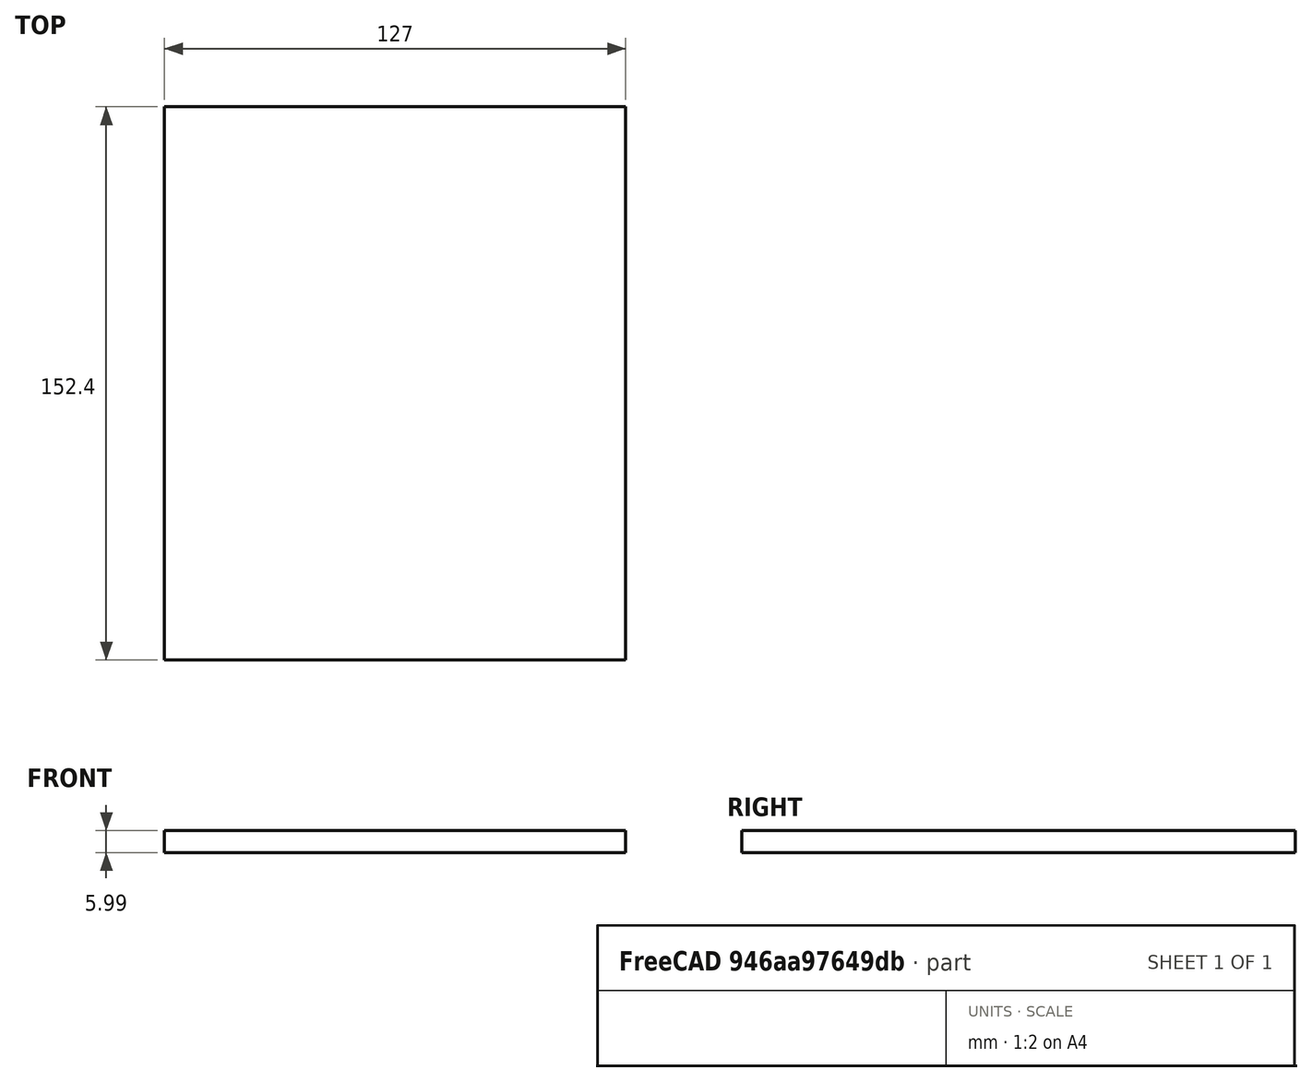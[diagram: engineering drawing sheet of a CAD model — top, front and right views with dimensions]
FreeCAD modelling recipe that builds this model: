
FCSTD DOCUMENT  (FreeCAD 0.19R24267 (Git))
Label: Inv1-P13
License: All rights reserved
LicenseURL: http://en.wikipedia.org/wiki/All_rights_reserved
objects: TechDraw::DrawViewDimension×3, Sketcher::SketchObject×2, TechDraw::DrawProjGroupItem×2, TechDraw::DrawHatch×2, TechDraw::DrawViewAnnotation×2, Part::Extrusion×1, TechDraw::DrawSVGTemplate×1, TechDraw::DrawProjGroup×1, TechDraw::DrawPage×1
note: 3 computed .brp shape members not serialized (recipe doc carries the construction recipe); baked Part::Feature solids carry a one-line shape summary decoded from their .brp

FEATURE [Sketcher::SketchObject] Sketch
  FullyConstrained = true
FEATURE [Sketcher::SketchObject] Sketch001
  FullyConstrained = false
  sketch-geometry (4):
    g0: LineSegment StartX=-70.7971 StartY=53.6303 StartZ=0 EndX=56.2029 EndY=53.6303 EndZ=0
    g1: LineSegment StartX=56.2029 StartY=53.6303 StartZ=0 EndX=56.2029 EndY=-98.7697 EndZ=0
    g2: LineSegment StartX=56.2029 StartY=-98.7697 StartZ=0 EndX=-70.7971 EndY=-98.7697 EndZ=0
    g3: LineSegment StartX=-70.7971 StartY=-98.7697 StartZ=0 EndX=-70.7971 EndY=53.6303 EndZ=0
  constraints (10):
    c: Coincident(g0,g1)
    c: Coincident(g1,g2)
    c: Coincident(g2,g3)
    c: Coincident(g3,g0)
    c: Horizontal(g0)
    c: Horizontal(g2)
    c: Vertical(g1)
    c: Vertical(g3)
    c: DistanceY(g3,g3) = 152.4
    c: DistanceX(g0,g0) = 127
FEATURE [Part::Extrusion] Extrude
  Base = -> Sketch001
  Dir = (0,0,1)
  DirMode = 2
  FaceMakerClass = Part::FaceMakerBullseye
  LengthFwd = 5.9944
  LengthRev = 0
  Solid = true
  Symmetric = false
FEATURE [TechDraw::DrawSVGTemplate] Template
  Height = 215.9
  Orientation = 1
  Width = 279.4
FEATURE [TechDraw::DrawProjGroupItem] ProjItem  label="Front"
  CoarseView = false
  Direction = (0,0,-1)
  Focus = 100
  HardHidden = false
  IsoCount = 0
  IsoHidden = false
  IsoVisible = false
  LockPosition = true
  Perspective = false
  Rotation = 0
  RotationVector = (1,0,0)
  Scale = 0.5
  ScaleType = 2
  SeamHidden = false
  SeamVisible = true
  SmoothHidden = false
  SmoothVisible = true
  Source = -> [Extrude]
  Type = 0
  X = 0
  XDirection = (1,0,0)
  Y = 0
FEATURE [TechDraw::DrawProjGroupItem] ProjItem001  label="Left"
  CoarseView = false
  Direction = (-1,0,-1e-16)
  Focus = 100
  HardHidden = false
  IsoCount = 0
  IsoHidden = false
  IsoVisible = false
  LockPosition = false
  Perspective = false
  Rotation = 0
  RotationVector = (1,0,0)
  Scale = 0.5
  ScaleType = 2
  SeamHidden = false
  SeamVisible = true
  SmoothHidden = false
  SmoothVisible = true
  Source = -> [Extrude]
  Type = 1
  X = 67.0707
  XDirection = (1e-16,0,-1)
  Y = 0
FEATURE [TechDraw::DrawProjGroup] ProjGroup
  Anchor = -> ProjItem
  AutoDistribute = true
  LockPosition = false
  ProjectionType = 0
  Rotation = 0
  Scale = 0.5
  ScaleType = 2
  Source = -> [Extrude]
  Views = -> [ProjItem,ProjItem001]
  X = 118.073
  Y = 114.57
  spacingX = 15.0114
  spacingY = 15.0114
FEATURE [TechDraw::DrawHatch] Hatch  label="HatchF0"
  HatchPattern = <path>
  Source = -> ProjItem [Face0]
FEATURE [TechDraw::DrawHatch] Hatch001  label="Hatch001F0"
  HatchPattern = <path>
  Source = -> ProjItem001 [Face0]
FEATURE [TechDraw::DrawViewDimension] Dimension
  Arbitrary = false
  ArbitraryTolerances = false
  EqualTolerance = true
  FormatSpec = %.3f
  FormatSpecOverTolerance = %+.3f
  FormatSpecUnderTolerance = %+.3f
  Inverted = false
  LockPosition = false
  MeasureType = 1
  OverTolerance = 0
  References2D = -> [ProjItem]
  Rotation = 0
  ScaleType = 0
  TheoreticalExact = false
  Type = 1
  UnderTolerance = 0
  X = -1.10341
  Y = -48.7663
FEATURE [TechDraw::DrawViewDimension] Dimension001
  Arbitrary = false
  ArbitraryTolerances = false
  EqualTolerance = true
  FormatSpec = %.3f
  FormatSpecOverTolerance = %+.3f
  FormatSpecUnderTolerance = %+.3f
  Inverted = false
  LockPosition = false
  MeasureType = 1
  OverTolerance = 0
  References2D = -> [ProjItem]
  Rotation = 0
  ScaleType = 0
  TheoreticalExact = false
  Type = 2
  UnderTolerance = 0
  X = 36.3475
  Y = 0.510837
FEATURE [TechDraw::DrawViewDimension] Dimension002
  Arbitrary = false
  ArbitraryTolerances = false
  EqualTolerance = true
  FormatSpec = %.3f
  FormatSpecOverTolerance = %+.3f
  FormatSpecUnderTolerance = %+.3f
  Inverted = false
  LockPosition = false
  MeasureType = 1
  OverTolerance = 0
  References2D = -> [ProjItem001]
  Rotation = 0
  ScaleType = 0
  TheoreticalExact = false
  Type = 1
  UnderTolerance = 0
  X = 22.8636
  Y = 25.1689
FEATURE [TechDraw::DrawViewAnnotation] Annotation
  Font = osifont
  LineSpace = 80
  LockPosition = false
  MaxWidth = -1
  Rotation = 0
  ScaleType = 0
  Text = Figure S1 (Inverted 1) | Panel 13 [stage door] | Quantity: 2
  TextSize = 5.0038
  TextStyle = 0
  X = 33.4201
  Y = 195.58
FEATURE [TechDraw::DrawViewAnnotation] Annotation002
  Font = osifont
  LineSpace = 80
  LockPosition = false
  MaxWidth = -1
  Rotation = 0
  ScaleType = 0
  Text = Units: Inches
  TextSize = 5.0038
  TextStyle = 0
  X = 259.08
  Y = 5.08
FEATURE [TechDraw::DrawPage] Page
  KeepUpdated = true
  NextBalloonIndex = 1
  ProjectionType = 0
  Template = -> Template
  Views = -> [ProjGroup,Dimension,Dimension001,Dimension002,Annotation,Annotation002]
note: 2 file-system paths scrubbed to <path> (originals preserved in the JSON sidecar)
